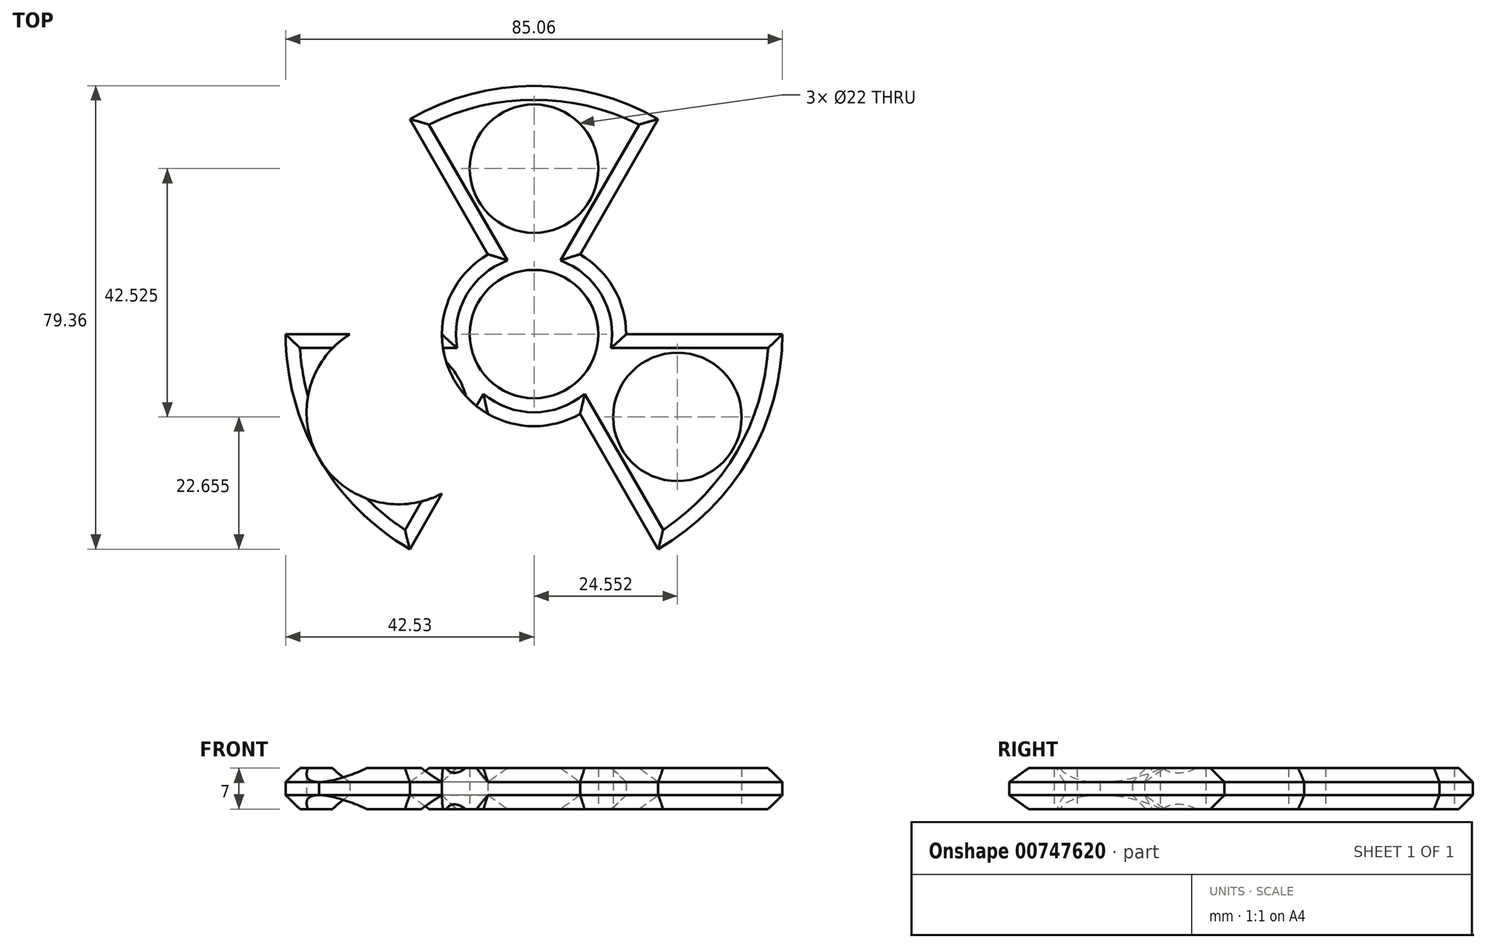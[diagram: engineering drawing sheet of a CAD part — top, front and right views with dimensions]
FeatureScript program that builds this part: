
annotation { "Feature Type Name" : "Feature", "Feature Type Description" : "" }
export const myFeature = defineFeature(function(context is Context, id is Id, definition is map)
    precondition{}
    {
        {
            var Q0;
            Q0=qCreatedBy(makeId("Top.planeOp"),FACE);
            var sketch = newSketch(context, id + "F0", { "sketchPlane" : qUnion([Q0])});
            skCircle(sketch, "E0", {"center": v(0, 0) * mm, "radius": 11 * mm});
            skCircle(sketch, "E1", {"center": v(0, 0) * mm, "radius": 15.76 * mm});
            skLineSegment(sketch, "E2", {"start": v(0, 0) * mm, "end": v(0, 26.76) * mm});
            skCircle(sketch, "E3", {"center": v(0, 26.76) * mm, "radius": 11 * mm});
            skArc(sketch, "E4", {"start": v(15.75, 27.29) * mm, "mid": v(0, 42.52) * mm, "end": v(-15.75, 27.29) * mm});
            skLineSegment(sketch, "E5", {"start": v(0, 26.76) * mm, "end": v(0, 46.59) * mm});
            skPoint(sketch, "E6", {"position": v(0, 42.52) * mm});
            skCircle(sketch, "E7", {"center": v(0, 0) * mm, "radius": 42.52 * mm});
            skLineSegment(sketch, "E8", {"start": v(0, 0) * mm, "end": v(21.26, 36.83) * mm});
            skLineSegment(sketch, "E9", {"start": v(0, 0) * mm, "end": v(-21.26, 36.83) * mm});
            skArc(sketch, "E10.trimOffspring", {"start": v(-8.33, 13.38) * mm, "mid": v(0, 11) * mm, "end": v(8.33, 13.38) * mm});
            skCircle(sketch, "E11.1.0", {"center": v(-23.18, -13.38) * mm, "radius": 11 * mm});
            skArc(sketch, "E11.1.1", {"start": v(-31.5, 0) * mm, "mid": v(-36.83, -21.26) * mm, "end": v(-15.75, -27.29) * mm});
            skLineSegment(sketch, "E11.1.2", {"start": v(0, 0) * mm, "end": v(-42.52, 0) * mm});
            skLineSegment(sketch, "E11.1.3", {"start": v(0, 0) * mm, "end": v(-21.26, -36.83) * mm});
            skCircle(sketch, "E11.2.0", {"center": v(23.18, -13.38) * mm, "radius": 11 * mm});
            skArc(sketch, "E11.2.1", {"start": v(15.75, -27.29) * mm, "mid": v(36.83, -21.26) * mm, "end": v(31.5, 0) * mm});
            skLineSegment(sketch, "E11.2.2", {"start": v(0, 0) * mm, "end": v(21.26, -36.83) * mm});
            skLineSegment(sketch, "E11.2.3", {"start": v(0, 0) * mm, "end": v(42.52, 0) * mm});
            skPoint(sketch, "E12", {"position": v(0, 28.35) * mm});
            skCircle(sketch, "E13", {"center": v(0, 28.35) * mm, "radius": 11 * mm});
            skCircle(sketch, "E14.1.0", {"center": v(-24.55, -14.17) * mm, "radius": 11 * mm});
            skCircle(sketch, "E14.2.0", {"center": v(24.55, -14.17) * mm, "radius": 11 * mm});
            skSolve(sketch);
        }
        {
            var Q0;
            {var subQ0=sQuery(id+"F0.wireOp",EDGE,"E8");var subQ1=sQuery(id+"F0.wireOp",EDGE,"E4");var subQ2=makeQuery(id+"F0.imprint","INTERSECT",VERTEX,{"derivedFrom":[subQ1,subQ0]});Q0=makeQuery(id+"F0.imprint","IMPRINT",FACE,{"disambiguationData":[TD([[makeQuery(id+"F0.imprint","IMPRINT",EDGE,{"disambiguationData":[TD([[subQ2,-1.0]])],"derivedFrom":subQ0}),1.0]])]});}
            var Q1;
            {var subQ0=sQuery(id+"F0.wireOp",EDGE,"E9");var subQ1=sQuery(id+"F0.wireOp",EDGE,"E4");var subQ2=makeQuery(id+"F0.imprint","INTERSECT",VERTEX,{"derivedFrom":[subQ1,subQ0]});Q1=makeQuery(id+"F0.imprint","IMPRINT",FACE,{"disambiguationData":[TD([[makeQuery(id+"F0.imprint","IMPRINT",EDGE,{"disambiguationData":[TD([[subQ2,-1.0]])],"derivedFrom":subQ0}),-1.0]])]});}
            var Q2;
            {var subQ0=sQuery(id+"F0.wireOp",EDGE,"E11.1.2");var subQ1=sQuery(id+"F0.wireOp",EDGE,"E7");var subQ2=makeQuery(id+"F0.imprint","INTERSECT",VERTEX,{"derivedFrom":[subQ1,subQ0]});Q2=makeQuery(id+"F0.imprint","IMPRINT",FACE,{"disambiguationData":[TD([[makeQuery(id+"F0.imprint","IMPRINT",EDGE,{"disambiguationData":[TD([[subQ2,-1.0]])],"derivedFrom":subQ1}),1.0]])]});}
            var Q3;
            {var subQ0=sQuery(id+"F0.wireOp",EDGE,"E11.1.3");var subQ1=sQuery(id+"F0.wireOp",EDGE,"E7");var subQ2=makeQuery(id+"F0.imprint","INTERSECT",VERTEX,{"derivedFrom":[subQ1,subQ0]});Q3=makeQuery(id+"F0.imprint","IMPRINT",FACE,{"disambiguationData":[TD([[makeQuery(id+"F0.imprint","IMPRINT",EDGE,{"disambiguationData":[TD([[subQ2,1.0]])],"derivedFrom":subQ1}),1.0]])]});}
            var Q4;
            {var subQ0=sQuery(id+"F0.wireOp",EDGE,"E11.2.2");var subQ1=sQuery(id+"F0.wireOp",EDGE,"E7");var subQ2=makeQuery(id+"F0.imprint","INTERSECT",VERTEX,{"derivedFrom":[subQ1,subQ0]});Q4=makeQuery(id+"F0.imprint","IMPRINT",FACE,{"disambiguationData":[TD([[makeQuery(id+"F0.imprint","IMPRINT",EDGE,{"disambiguationData":[TD([[subQ2,-1.0]])],"derivedFrom":subQ1}),1.0]])]});}
            var Q5;
            {var subQ0=sQuery(id+"F0.wireOp",EDGE,"E11.2.3");var subQ1=sQuery(id+"F0.wireOp",EDGE,"E7");var subQ2=makeQuery(id+"F0.imprint","INTERSECT",VERTEX,{"derivedFrom":[subQ1,subQ0]});Q5=makeQuery(id+"F0.imprint","IMPRINT",FACE,{"disambiguationData":[TD([[makeQuery(id+"F0.imprint","IMPRINT",EDGE,{"disambiguationData":[TD([[subQ2,1.0]])],"derivedFrom":subQ1}),1.0]])]});}
            var Q6;
            {var subQ3=sQuery(id+"F0.wireOp",EDGE,"E4");var subQ5=sQuery(id+"F0.wireOp",EDGE,"E8");var subQ6=makeQuery(id+"F0.imprint","INTERSECT",VERTEX,{"derivedFrom":[subQ3,subQ5]});Q6=makeQuery(id+"F0.imprint","IMPRINT",FACE,{"disambiguationData":[TD([[makeQuery(id+"F0.imprint","IMPRINT",EDGE,{"disambiguationData":[TD([[subQ6,1.0]])],"derivedFrom":subQ5}),1.0]])]});}
            var Q7;
            {var subQ0=sQuery(id+"F0.wireOp",EDGE,"E9");var subQ1=sQuery(id+"F0.wireOp",EDGE,"E4");var subQ2=makeQuery(id+"F0.imprint","INTERSECT",VERTEX,{"derivedFrom":[subQ1,subQ0]});Q7=makeQuery(id+"F0.imprint","IMPRINT",FACE,{"disambiguationData":[TD([[makeQuery(id+"F0.imprint","IMPRINT",EDGE,{"disambiguationData":[TD([[subQ2,1.0]])],"derivedFrom":subQ0}),-1.0]])]});}
            var Q8;
            {var subQ4=sQuery(id+"F0.wireOp",EDGE,"E11.1.0");Q8=makeQuery(id+"F0.imprint","IMPRINT",FACE,{"disambiguationData":[TD([[makeQuery(id+"F0.imprint","IMPRINT",EDGE,{"derivedFrom":subQ4}),-1.0]])]});}
            var Q9;
            {var subQ4=sQuery(id+"F0.wireOp",EDGE,"E11.2.0");Q9=makeQuery(id+"F0.imprint","IMPRINT",FACE,{"disambiguationData":[TD([[makeQuery(id+"F0.imprint","IMPRINT",EDGE,{"derivedFrom":subQ4}),-1.0]])]});}
            var Q10;
            {var subQ2=sQuery(id+"F0.wireOp",EDGE,"E11.1.2");var subQ4=sQuery(id+"F0.wireOp",EDGE,"E0");var subQ5=makeQuery(id+"F0.imprint","INTERSECT",VERTEX,{"derivedFrom":[subQ4,subQ2]});Q10=makeQuery(id+"F0.imprint","IMPRINT",FACE,{"disambiguationData":[TD([[makeQuery(id+"F0.imprint","IMPRINT",EDGE,{"disambiguationData":[TD([[subQ5,-1.0]])],"derivedFrom":subQ4}),-1.0]])]});}
            var Q11;
            {var subQ0=sQuery(id+"F0.wireOp",EDGE,"E11.1.3");var subQ1=sQuery(id+"F0.wireOp",EDGE,"E0");var subQ2=makeQuery(id+"F0.imprint","INTERSECT",VERTEX,{"derivedFrom":[subQ1,subQ0]});Q11=makeQuery(id+"F0.imprint","IMPRINT",FACE,{"disambiguationData":[TD([[makeQuery(id+"F0.imprint","IMPRINT",EDGE,{"disambiguationData":[TD([[subQ2,-1.0]])],"derivedFrom":subQ1}),-1.0]])]});}
            var Q12;
            {var subQ1=sQuery(id+"F0.wireOp",EDGE,"E0");var subQ6=sQuery(id+"F0.wireOp",EDGE,"E11.2.3");var subQ8=makeQuery(id+"F0.imprint","INTERSECT",VERTEX,{"derivedFrom":[subQ1,subQ6]});Q12=makeQuery(id+"F0.imprint","IMPRINT",FACE,{"disambiguationData":[TD([[makeQuery(id+"F0.imprint","IMPRINT",EDGE,{"disambiguationData":[TD([[subQ8,1.0]])],"derivedFrom":subQ1}),-1.0]])]});}
            var Q13;
            {var subQ3=sQuery(id+"F0.wireOp",EDGE,"E8");var subQ5=sQuery(id+"F0.wireOp",EDGE,"E0");var subQ6=makeQuery(id+"F0.imprint","INTERSECT",VERTEX,{"derivedFrom":[subQ5,subQ3]});Q13=makeQuery(id+"F0.imprint","IMPRINT",FACE,{"disambiguationData":[TD([[makeQuery(id+"F0.imprint","IMPRINT",EDGE,{"disambiguationData":[TD([[subQ6,1.0]])],"derivedFrom":subQ5}),-1.0]])]});}
            var Q14;
            {var subQ0=sQuery(id+"F0.wireOp",EDGE,"E8");var subQ1=sQuery(id+"F0.wireOp",EDGE,"E0");var subQ2=makeQuery(id+"F0.imprint","INTERSECT",VERTEX,{"derivedFrom":[subQ1,subQ0]});Q14=makeQuery(id+"F0.imprint","IMPRINT",FACE,{"disambiguationData":[TD([[makeQuery(id+"F0.imprint","IMPRINT",EDGE,{"disambiguationData":[TD([[subQ2,-1.0]])],"derivedFrom":subQ0}),1.0]])]});}
            var Q15;
            {var subQ0=sQuery(id+"F0.wireOp",EDGE,"E8");var subQ1=sQuery(id+"F0.wireOp",EDGE,"E1");var subQ2=makeQuery(id+"F0.imprint","INTERSECT",VERTEX,{"derivedFrom":[subQ1,subQ0]});Q15=makeQuery(id+"F0.imprint","IMPRINT",FACE,{"disambiguationData":[TD([[makeQuery(id+"F0.imprint","IMPRINT",EDGE,{"disambiguationData":[TD([[subQ2,1.0]])],"derivedFrom":subQ0}),1.0]])]});}
            var Q16;
            {var subQ0=sQuery(id+"F0.wireOp",EDGE,"E9");var subQ1=sQuery(id+"F0.wireOp",EDGE,"E1");var subQ2=makeQuery(id+"F0.imprint","INTERSECT",VERTEX,{"derivedFrom":[subQ1,subQ0]});Q16=makeQuery(id+"F0.imprint","IMPRINT",FACE,{"disambiguationData":[TD([[makeQuery(id+"F0.imprint","IMPRINT",EDGE,{"disambiguationData":[TD([[subQ2,1.0]])],"derivedFrom":subQ0}),-1.0]])]});}
            var Q17;
            {var subQ0=sQuery(id+"F0.wireOp",EDGE,"E9");var subQ1=sQuery(id+"F0.wireOp",EDGE,"E0");var subQ2=makeQuery(id+"F0.imprint","INTERSECT",VERTEX,{"derivedFrom":[subQ1,subQ0]});Q17=makeQuery(id+"F0.imprint","IMPRINT",FACE,{"disambiguationData":[TD([[makeQuery(id+"F0.imprint","IMPRINT",EDGE,{"disambiguationData":[TD([[subQ2,-1.0]])],"derivedFrom":subQ0}),-1.0]])]});}
            var Q18;
            {var subQ3=sQuery(id+"F0.wireOp",EDGE,"E9");var subQ5=sQuery(id+"F0.wireOp",EDGE,"E0");var subQ6=makeQuery(id+"F0.imprint","INTERSECT",VERTEX,{"derivedFrom":[subQ5,subQ3]});Q18=makeQuery(id+"F0.imprint","IMPRINT",FACE,{"disambiguationData":[TD([[makeQuery(id+"F0.imprint","IMPRINT",EDGE,{"disambiguationData":[TD([[subQ6,-1.0]])],"derivedFrom":subQ5}),-1.0]])]});}
            var Q19;
            {var subQ0=sQuery(id+"F0.wireOp",EDGE,"E8");var subQ1=sQuery(id+"F0.wireOp",EDGE,"E0");var subQ2=makeQuery(id+"F0.imprint","INTERSECT",VERTEX,{"derivedFrom":[subQ1,subQ0]});Q19=makeQuery(id+"F0.imprint","IMPRINT",FACE,{"disambiguationData":[TD([[makeQuery(id+"F0.imprint","IMPRINT",EDGE,{"disambiguationData":[TD([[subQ2,1.0]])],"derivedFrom":subQ1}),1.0]])]});}
            var Q20;
            {var subQ0=sQuery(id+"F0.wireOp",EDGE,"E8");var subQ1=sQuery(id+"F0.wireOp",EDGE,"E0");var subQ2=makeQuery(id+"F0.imprint","INTERSECT",VERTEX,{"derivedFrom":[subQ1,subQ0]});Q20=makeQuery(id+"F0.imprint","IMPRINT",FACE,{"disambiguationData":[TD([[makeQuery(id+"F0.imprint","IMPRINT",EDGE,{"disambiguationData":[TD([[subQ2,-1.0]])],"derivedFrom":subQ1}),1.0]])]});}
            var Q21;
            {var subQ0=sQuery(id+"F0.wireOp",EDGE,"E9");var subQ1=sQuery(id+"F0.wireOp",EDGE,"E0");var subQ2=makeQuery(id+"F0.imprint","INTERSECT",VERTEX,{"derivedFrom":[subQ1,subQ0]});Q21=makeQuery(id+"F0.imprint","IMPRINT",FACE,{"disambiguationData":[TD([[makeQuery(id+"F0.imprint","IMPRINT",EDGE,{"disambiguationData":[TD([[subQ2,1.0]])],"derivedFrom":subQ1}),1.0]])]});}
            var Q22;
            {var subQ0=sQuery(id+"F0.wireOp",EDGE,"E9");var subQ1=sQuery(id+"F0.wireOp",EDGE,"E0");var subQ2=makeQuery(id+"F0.imprint","INTERSECT",VERTEX,{"derivedFrom":[subQ1,subQ0]});Q22=makeQuery(id+"F0.imprint","IMPRINT",FACE,{"disambiguationData":[TD([[makeQuery(id+"F0.imprint","IMPRINT",EDGE,{"disambiguationData":[TD([[subQ2,-1.0]])],"derivedFrom":subQ1}),1.0]])]});}
            var Q23;
            {var subQ0=sQuery(id+"F0.wireOp",EDGE,"E11.1.2");var subQ1=sQuery(id+"F0.wireOp",EDGE,"E0");var subQ2=makeQuery(id+"F0.imprint","INTERSECT",VERTEX,{"derivedFrom":[subQ1,subQ0]});Q23=makeQuery(id+"F0.imprint","IMPRINT",FACE,{"disambiguationData":[TD([[makeQuery(id+"F0.imprint","IMPRINT",EDGE,{"disambiguationData":[TD([[subQ2,-1.0]])],"derivedFrom":subQ1}),1.0]])]});}
            var Q24;
            {var subQ0=sQuery(id+"F0.wireOp",EDGE,"E11.2.3");var subQ1=sQuery(id+"F0.wireOp",EDGE,"E0");var subQ2=makeQuery(id+"F0.imprint","INTERSECT",VERTEX,{"derivedFrom":[subQ1,subQ0]});Q24=makeQuery(id+"F0.imprint","IMPRINT",FACE,{"disambiguationData":[TD([[makeQuery(id+"F0.imprint","IMPRINT",EDGE,{"disambiguationData":[TD([[subQ2,1.0]])],"derivedFrom":subQ1}),1.0]])]});}
            var Q25;
            Q25=makeQuery(id+"F0.imprint","IMPRINT",FACE,{"disambiguationData":[TD([[makeQuery(id+"F0.imprint","IMPRINT",EDGE,{"derivedFrom":sQuery(id+"F0.wireOp",EDGE,"E11.2.0")}),1.0]])]});
            var Q26;
            Q26=makeQuery(id+"F0.imprint","IMPRINT",FACE,{"disambiguationData":[TD([[makeQuery(id+"F0.imprint","IMPRINT",EDGE,{"derivedFrom":sQuery(id+"F0.wireOp",EDGE,"E11.1.0")}),1.0]])]});
            var Q27;
            {var subQ0=sQuery(id+"F0.wireOp",EDGE,"E5");var subQ1=sQuery(id+"F0.wireOp",EDGE,"E2");var subQ2=makeQuery(id+"F0.imprint","INTERSECT",VERTEX,{"derivedFrom":[subQ1,subQ0]});Q27=makeQuery(id+"F0.imprint","IMPRINT",FACE,{"disambiguationData":[TD([[makeQuery(id+"F0.imprint","IMPRINT",EDGE,{"disambiguationData":[TD([[subQ2,-1.0]])],"derivedFrom":subQ0}),1.0]])]});}
            var Q28;
            {var subQ0=sQuery(id+"F0.wireOp",EDGE,"E11.1.3");var subQ1=sQuery(id+"F0.wireOp",EDGE,"E0");var subQ2=makeQuery(id+"F0.imprint","INTERSECT",VERTEX,{"derivedFrom":[subQ1,subQ0]});Q28=makeQuery(id+"F0.imprint","IMPRINT",FACE,{"disambiguationData":[TD([[makeQuery(id+"F0.imprint","IMPRINT",EDGE,{"disambiguationData":[TD([[subQ2,-1.0]])],"derivedFrom":subQ1}),1.0]])]});}
            var Q29;
            {var subQ0=sQuery(id+"F0.wireOp",EDGE,"E10.trimOffspring");var subQ1=sQuery(id+"F0.wireOp",EDGE,"E1");var subQ2=makeQuery(id+"F0.imprint","INTERSECT",VERTEX,{"disambiguationData":[OD(1.0)],"derivedFrom":[subQ1,subQ0]});Q29=makeQuery(id+"F0.imprint","IMPRINT",FACE,{"disambiguationData":[TD([[makeQuery(id+"F0.imprint","IMPRINT",EDGE,{"disambiguationData":[TD([[subQ2,-1.0]])],"derivedFrom":subQ1}),1.0]])]});}
            var Q30;
            {var subQ0=sQuery(id+"F0.wireOp",EDGE,"E10.trimOffspring");var subQ1=sQuery(id+"F0.wireOp",EDGE,"E1");var subQ2=makeQuery(id+"F0.imprint","INTERSECT",VERTEX,{"disambiguationData":[OD(0.0)],"derivedFrom":[subQ1,subQ0]});Q30=makeQuery(id+"F0.imprint","IMPRINT",FACE,{"disambiguationData":[TD([[makeQuery(id+"F0.imprint","IMPRINT",EDGE,{"disambiguationData":[TD([[subQ2,1.0]])],"derivedFrom":subQ1}),1.0]])]});}
            var Q31;
            {var subQ0=sQuery(id+"F0.wireOp",EDGE,"E13");var subQ1=sQuery(id+"F0.wireOp",EDGE,"E2");var subQ2=makeQuery(id+"F0.imprint","INTERSECT",VERTEX,{"derivedFrom":[subQ1,subQ0]});Q31=makeQuery(id+"F0.imprint","IMPRINT",FACE,{"disambiguationData":[TD([[makeQuery(id+"F0.imprint","IMPRINT",EDGE,{"disambiguationData":[TD([[subQ2,-1.0]])],"derivedFrom":subQ0}),-1.0]])]});}
            var Q32;
            {var subQ0=sQuery(id+"F0.wireOp",EDGE,"E5");var subQ1=sQuery(id+"F0.wireOp",EDGE,"E3");var subQ2=makeQuery(id+"F0.imprint","INTERSECT",VERTEX,{"derivedFrom":[subQ1,subQ0]});Q32=makeQuery(id+"F0.imprint","IMPRINT",FACE,{"disambiguationData":[TD([[makeQuery(id+"F0.imprint","IMPRINT",EDGE,{"disambiguationData":[TD([[subQ2,1.0]])],"derivedFrom":subQ1}),-1.0]])]});}
            var Q33;
            {var subQ0=sQuery(id+"F0.wireOp",EDGE,"E13");var subQ1=sQuery(id+"F0.wireOp",EDGE,"E2");var subQ2=makeQuery(id+"F0.imprint","INTERSECT",VERTEX,{"derivedFrom":[subQ1,subQ0]});Q33=makeQuery(id+"F0.imprint","IMPRINT",FACE,{"disambiguationData":[TD([[makeQuery(id+"F0.imprint","IMPRINT",EDGE,{"disambiguationData":[TD([[subQ2,1.0]])],"derivedFrom":subQ0}),-1.0]])]});}
            var Q34;
            {var subQ0=sQuery(id+"F0.wireOp",EDGE,"E5");var subQ1=sQuery(id+"F0.wireOp",EDGE,"E3");var subQ2=makeQuery(id+"F0.imprint","INTERSECT",VERTEX,{"derivedFrom":[subQ1,subQ0]});Q34=makeQuery(id+"F0.imprint","IMPRINT",FACE,{"disambiguationData":[TD([[makeQuery(id+"F0.imprint","IMPRINT",EDGE,{"disambiguationData":[TD([[subQ2,-1.0]])],"derivedFrom":subQ1}),-1.0]])]});}
            var Q35;
            {var subQ0=sQuery(id+"F0.wireOp",EDGE,"E5");var subQ1=sQuery(id+"F0.wireOp",EDGE,"E2");var subQ2=makeQuery(id+"F0.imprint","INTERSECT",VERTEX,{"derivedFrom":[subQ1,subQ0]});Q35=makeQuery(id+"F0.imprint","IMPRINT",FACE,{"disambiguationData":[TD([[makeQuery(id+"F0.imprint","IMPRINT",EDGE,{"disambiguationData":[TD([[subQ2,1.0]])],"derivedFrom":subQ1}),-1.0]])]});}
            var Q36;
            {var subQ0=sQuery(id+"F0.wireOp",EDGE,"E14.2.0");var subQ1=sQuery(id+"F0.wireOp",EDGE,"E11.2.0");var subQ2=makeQuery(id+"F0.imprint","INTERSECT",VERTEX,{"disambiguationData":[OD(0.0)],"derivedFrom":[subQ1,subQ0]});Q36=makeQuery(id+"F0.imprint","IMPRINT",FACE,{"disambiguationData":[TD([[makeQuery(id+"F0.imprint","IMPRINT",EDGE,{"disambiguationData":[TD([[subQ2,1.0]])],"derivedFrom":subQ1}),-1.0]])]});}
            var Q37;
            {var subQ0=sQuery(id+"F0.wireOp",EDGE,"E14.2.0");var subQ1=sQuery(id+"F0.wireOp",EDGE,"E11.2.0");var subQ2=makeQuery(id+"F0.imprint","INTERSECT",VERTEX,{"disambiguationData":[OD(0.0)],"derivedFrom":[subQ1,subQ0]});Q37=makeQuery(id+"F0.imprint","IMPRINT",FACE,{"disambiguationData":[TD([[makeQuery(id+"F0.imprint","IMPRINT",EDGE,{"disambiguationData":[TD([[subQ2,1.0]])],"derivedFrom":subQ1}),1.0]])]});}
            var Q38;
            {var subQ0=sQuery(id+"F0.wireOp",EDGE,"E14.1.0");var subQ1=sQuery(id+"F0.wireOp",EDGE,"E11.1.0");var subQ2=makeQuery(id+"F0.imprint","INTERSECT",VERTEX,{"disambiguationData":[OD(0.0)],"derivedFrom":[subQ1,subQ0]});Q38=makeQuery(id+"F0.imprint","IMPRINT",FACE,{"disambiguationData":[TD([[makeQuery(id+"F0.imprint","IMPRINT",EDGE,{"disambiguationData":[TD([[subQ2,1.0]])],"derivedFrom":subQ1}),1.0]])]});}
            var Q39;
            {var subQ0=sQuery(id+"F0.wireOp",EDGE,"E14.1.0");var subQ1=sQuery(id+"F0.wireOp",EDGE,"E11.1.0");var subQ2=makeQuery(id+"F0.imprint","INTERSECT",VERTEX,{"disambiguationData":[OD(0.0)],"derivedFrom":[subQ1,subQ0]});Q39=makeQuery(id+"F0.imprint","IMPRINT",FACE,{"disambiguationData":[TD([[makeQuery(id+"F0.imprint","IMPRINT",EDGE,{"disambiguationData":[TD([[subQ2,1.0]])],"derivedFrom":subQ1}),-1.0]])]});}
            extrude(context, id + "F1", {"entities" : qUnion([Q0, Q1, Q2, Q3, Q4, Q5, Q6, Q7, Q8, Q9, Q10, Q11, Q12, Q13, Q14, Q15, Q16, Q17, Q18, Q19, Q20, Q21, Q22, Q23, Q24, Q25, Q26, Q27, Q28, Q29, Q30, Q31, Q32, Q33, Q34, Q35, Q36, Q37, Q38, Q39]), "depth" : 7 * mm, "offsetDistance" : 25.4 * mm});
        }
        {
            var Q0;
            Q0=makeQuery(id+"F1.opExtrude","CAP_FACE",FACE,{"disambiguationData":[OSD([sQuery(id+"F0.wireOp",EDGE,"E1"),sQuery(id+"F0.wireOp",EDGE,"E7"),sQuery(id+"F0.wireOp",EDGE,"E8"),sQuery(id+"F0.wireOp",EDGE,"E9"),sQuery(id+"F0.wireOp",EDGE,"E11.1.2"),sQuery(id+"F0.wireOp",EDGE,"E11.1.3"),sQuery(id+"F0.wireOp",EDGE,"E11.2.2"),sQuery(id+"F0.wireOp",EDGE,"E11.2.3")])],"isStart":false});
            var Q1;
            Q1=makeQuery(id+"F1.opExtrude","CAP_FACE",FACE,{"disambiguationData":[OSD([sQuery(id+"F0.wireOp",EDGE,"E1"),sQuery(id+"F0.wireOp",EDGE,"E7"),sQuery(id+"F0.wireOp",EDGE,"E8"),sQuery(id+"F0.wireOp",EDGE,"E9"),sQuery(id+"F0.wireOp",EDGE,"E11.1.2"),sQuery(id+"F0.wireOp",EDGE,"E11.1.3"),sQuery(id+"F0.wireOp",EDGE,"E11.2.2"),sQuery(id+"F0.wireOp",EDGE,"E11.2.3")])],"isStart":true});
            chamfer(context, id + "F2", {"entities" : qUnion([Q0, Q1]), "width" : 2.38 * mm, "tangentPropagation" : true});
        }
        {
            var Q0;
            {var subQ0=sQuery(id+"F0.wireOp",EDGE,"E14.1.0");var subQ1=sQuery(id+"F0.wireOp",EDGE,"E11.1.0");var subQ2=makeQuery(id+"F0.imprint","INTERSECT",VERTEX,{"disambiguationData":[OD(0.0)],"derivedFrom":[subQ1,subQ0]});Q0=makeQuery(id+"F0.imprint","IMPRINT",FACE,{"disambiguationData":[TD([[makeQuery(id+"F0.imprint","IMPRINT",EDGE,{"disambiguationData":[TD([[subQ2,1.0]])],"derivedFrom":subQ1}),-1.0]])]});}
            var Q1;
            {var subQ0=sQuery(id+"F0.wireOp",EDGE,"E14.1.0");var subQ1=sQuery(id+"F0.wireOp",EDGE,"E11.1.0");var subQ2=makeQuery(id+"F0.imprint","INTERSECT",VERTEX,{"disambiguationData":[OD(0.0)],"derivedFrom":[subQ1,subQ0]});Q1=makeQuery(id+"F0.imprint","IMPRINT",FACE,{"disambiguationData":[TD([[makeQuery(id+"F0.imprint","IMPRINT",EDGE,{"disambiguationData":[TD([[subQ2,1.0]])],"derivedFrom":subQ1}),1.0]])]});}
            var Q2;
            {var subQ0=sQuery(id+"F0.wireOp",EDGE,"E14.2.0");var subQ1=sQuery(id+"F0.wireOp",EDGE,"E11.2.0");var subQ2=makeQuery(id+"F0.imprint","INTERSECT",VERTEX,{"disambiguationData":[OD(0.0)],"derivedFrom":[subQ1,subQ0]});Q2=makeQuery(id+"F0.imprint","IMPRINT",FACE,{"disambiguationData":[TD([[makeQuery(id+"F0.imprint","IMPRINT",EDGE,{"disambiguationData":[TD([[subQ2,1.0]])],"derivedFrom":subQ1}),-1.0]])]});}
            var Q3;
            {var subQ0=sQuery(id+"F0.wireOp",EDGE,"E14.2.0");var subQ1=sQuery(id+"F0.wireOp",EDGE,"E11.2.0");var subQ2=makeQuery(id+"F0.imprint","INTERSECT",VERTEX,{"disambiguationData":[OD(0.0)],"derivedFrom":[subQ1,subQ0]});Q3=makeQuery(id+"F0.imprint","IMPRINT",FACE,{"disambiguationData":[TD([[makeQuery(id+"F0.imprint","IMPRINT",EDGE,{"disambiguationData":[TD([[subQ2,1.0]])],"derivedFrom":subQ1}),1.0]])]});}
            var Q4;
            {var subQ0=sQuery(id+"F0.wireOp",EDGE,"E5");var subQ1=sQuery(id+"F0.wireOp",EDGE,"E2");var subQ2=makeQuery(id+"F0.imprint","INTERSECT",VERTEX,{"derivedFrom":[subQ1,subQ0]});Q4=makeQuery(id+"F0.imprint","IMPRINT",FACE,{"disambiguationData":[TD([[makeQuery(id+"F0.imprint","IMPRINT",EDGE,{"disambiguationData":[TD([[subQ2,1.0]])],"derivedFrom":subQ1}),-1.0]])]});}
            var Q5;
            {var subQ0=sQuery(id+"F0.wireOp",EDGE,"E5");var subQ1=sQuery(id+"F0.wireOp",EDGE,"E3");var subQ2=makeQuery(id+"F0.imprint","INTERSECT",VERTEX,{"derivedFrom":[subQ1,subQ0]});Q5=makeQuery(id+"F0.imprint","IMPRINT",FACE,{"disambiguationData":[TD([[makeQuery(id+"F0.imprint","IMPRINT",EDGE,{"disambiguationData":[TD([[subQ2,1.0]])],"derivedFrom":subQ1}),-1.0]])]});}
            var Q6;
            {var subQ0=sQuery(id+"F0.wireOp",EDGE,"E5");var subQ1=sQuery(id+"F0.wireOp",EDGE,"E2");var subQ2=makeQuery(id+"F0.imprint","INTERSECT",VERTEX,{"derivedFrom":[subQ1,subQ0]});Q6=makeQuery(id+"F0.imprint","IMPRINT",FACE,{"disambiguationData":[TD([[makeQuery(id+"F0.imprint","IMPRINT",EDGE,{"disambiguationData":[TD([[subQ2,1.0]])],"derivedFrom":subQ1}),1.0]])]});}
            var Q7;
            {var subQ0=sQuery(id+"F0.wireOp",EDGE,"E5");var subQ1=sQuery(id+"F0.wireOp",EDGE,"E3");var subQ2=makeQuery(id+"F0.imprint","INTERSECT",VERTEX,{"derivedFrom":[subQ1,subQ0]});Q7=makeQuery(id+"F0.imprint","IMPRINT",FACE,{"disambiguationData":[TD([[makeQuery(id+"F0.imprint","IMPRINT",EDGE,{"disambiguationData":[TD([[subQ2,-1.0]])],"derivedFrom":subQ1}),-1.0]])]});}
            var Q8;
            {var subQ0=sQuery(id+"F0.wireOp",EDGE,"E11.1.3");var subQ1=sQuery(id+"F0.wireOp",EDGE,"E0");var subQ2=makeQuery(id+"F0.imprint","INTERSECT",VERTEX,{"derivedFrom":[subQ1,subQ0]});Q8=makeQuery(id+"F0.imprint","IMPRINT",FACE,{"disambiguationData":[TD([[makeQuery(id+"F0.imprint","IMPRINT",EDGE,{"disambiguationData":[TD([[subQ2,-1.0]])],"derivedFrom":subQ1}),1.0]])]});}
            var Q9;
            {var subQ0=sQuery(id+"F0.wireOp",EDGE,"E11.1.2");var subQ1=sQuery(id+"F0.wireOp",EDGE,"E0");var subQ2=makeQuery(id+"F0.imprint","INTERSECT",VERTEX,{"derivedFrom":[subQ1,subQ0]});Q9=makeQuery(id+"F0.imprint","IMPRINT",FACE,{"disambiguationData":[TD([[makeQuery(id+"F0.imprint","IMPRINT",EDGE,{"disambiguationData":[TD([[subQ2,-1.0]])],"derivedFrom":subQ1}),1.0]])]});}
            var Q10;
            {var subQ0=sQuery(id+"F0.wireOp",EDGE,"E9");var subQ1=sQuery(id+"F0.wireOp",EDGE,"E0");var subQ2=makeQuery(id+"F0.imprint","INTERSECT",VERTEX,{"derivedFrom":[subQ1,subQ0]});Q10=makeQuery(id+"F0.imprint","IMPRINT",FACE,{"disambiguationData":[TD([[makeQuery(id+"F0.imprint","IMPRINT",EDGE,{"disambiguationData":[TD([[subQ2,-1.0]])],"derivedFrom":subQ1}),1.0]])]});}
            var Q11;
            {var subQ0=sQuery(id+"F0.wireOp",EDGE,"E9");var subQ1=sQuery(id+"F0.wireOp",EDGE,"E0");var subQ2=makeQuery(id+"F0.imprint","INTERSECT",VERTEX,{"derivedFrom":[subQ1,subQ0]});Q11=makeQuery(id+"F0.imprint","IMPRINT",FACE,{"disambiguationData":[TD([[makeQuery(id+"F0.imprint","IMPRINT",EDGE,{"disambiguationData":[TD([[subQ2,1.0]])],"derivedFrom":subQ1}),1.0]])]});}
            var Q12;
            {var subQ0=sQuery(id+"F0.wireOp",EDGE,"E8");var subQ1=sQuery(id+"F0.wireOp",EDGE,"E0");var subQ2=makeQuery(id+"F0.imprint","INTERSECT",VERTEX,{"derivedFrom":[subQ1,subQ0]});Q12=makeQuery(id+"F0.imprint","IMPRINT",FACE,{"disambiguationData":[TD([[makeQuery(id+"F0.imprint","IMPRINT",EDGE,{"disambiguationData":[TD([[subQ2,-1.0]])],"derivedFrom":subQ1}),1.0]])]});}
            var Q13;
            {var subQ0=sQuery(id+"F0.wireOp",EDGE,"E8");var subQ1=sQuery(id+"F0.wireOp",EDGE,"E0");var subQ2=makeQuery(id+"F0.imprint","INTERSECT",VERTEX,{"derivedFrom":[subQ1,subQ0]});Q13=makeQuery(id+"F0.imprint","IMPRINT",FACE,{"disambiguationData":[TD([[makeQuery(id+"F0.imprint","IMPRINT",EDGE,{"disambiguationData":[TD([[subQ2,1.0]])],"derivedFrom":subQ1}),1.0]])]});}
            var Q14;
            {var subQ0=sQuery(id+"F0.wireOp",EDGE,"E11.2.3");var subQ1=sQuery(id+"F0.wireOp",EDGE,"E0");var subQ2=makeQuery(id+"F0.imprint","INTERSECT",VERTEX,{"derivedFrom":[subQ1,subQ0]});Q14=makeQuery(id+"F0.imprint","IMPRINT",FACE,{"disambiguationData":[TD([[makeQuery(id+"F0.imprint","IMPRINT",EDGE,{"disambiguationData":[TD([[subQ2,1.0]])],"derivedFrom":subQ1}),1.0]])]});}
            extrude(context, id + "F3", {"entities" : qUnion([Q0, Q1, Q2, Q3, Q4, Q5, Q6, Q7, Q8, Q9, Q10, Q11, Q12, Q13, Q14]), "operationType" : NewBodyOperationType.REMOVE, "endBound" : BoundingType.THROUGH_ALL, "depth" : 25.4 * mm, "offsetDistance" : 25.4 * mm});
        }
    });
